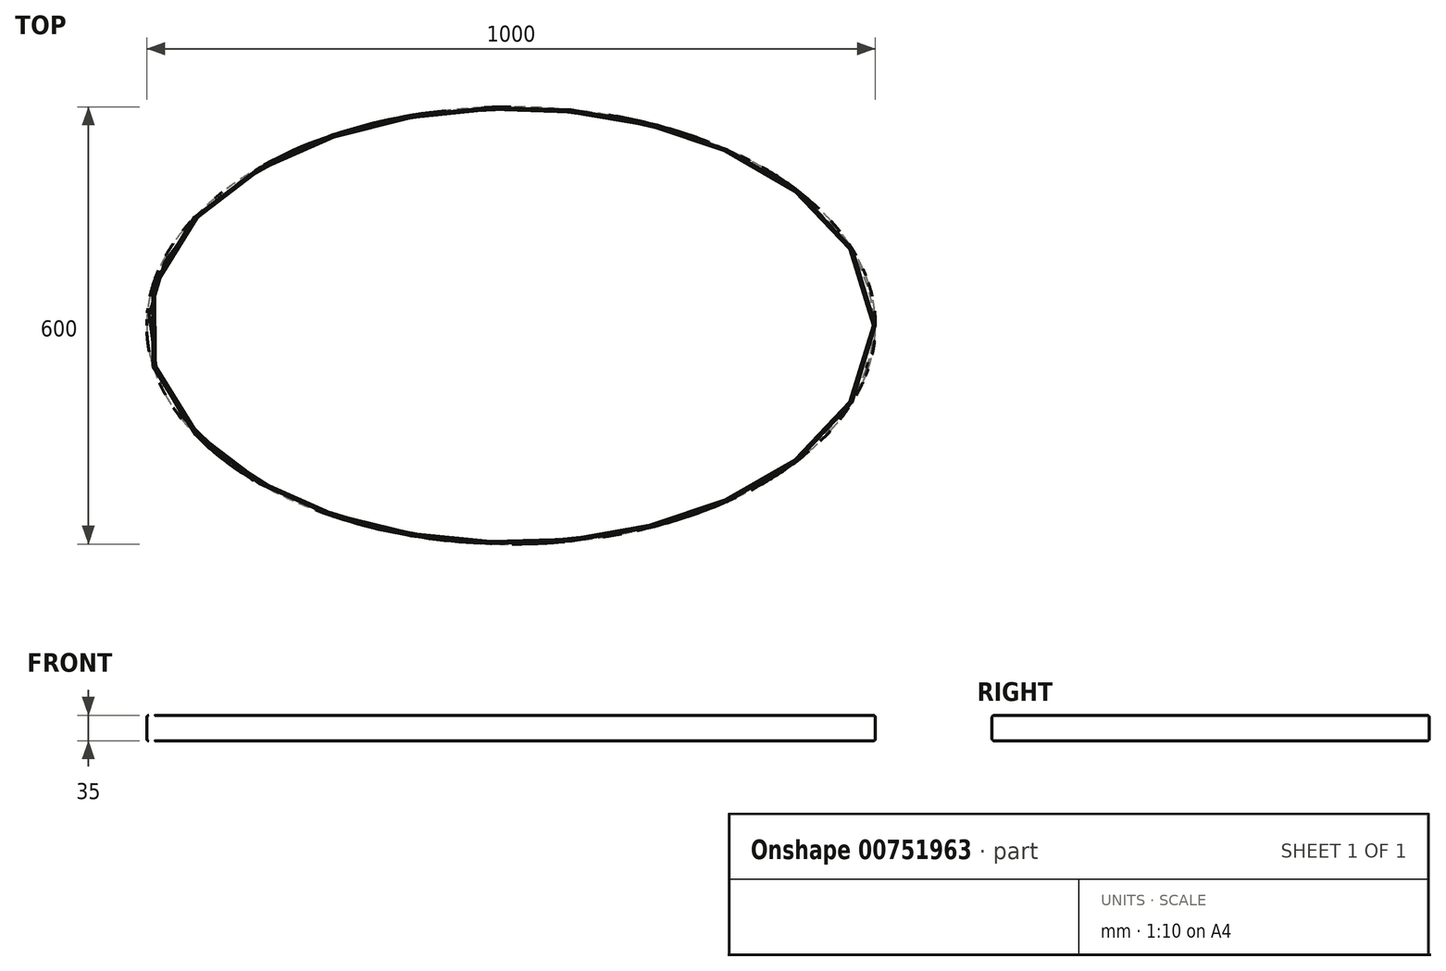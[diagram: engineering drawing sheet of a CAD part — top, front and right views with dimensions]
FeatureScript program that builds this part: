
annotation { "Feature Type Name" : "Feature", "Feature Type Description" : "" }
export const myFeature = defineFeature(function(context is Context, id is Id, definition is map)
    precondition{}
    {
        {
            var Q0;
            Q0=qCreatedBy(makeId("Top.planeOp"),FACE);
            var sketch = newSketch(context, id + "F0", { "sketchPlane" : qUnion([Q0])});
            skEllipse(sketch, "E0", {"center": v(0, 0) * mm, "majorRadius": 500 * mm, "minorRadius": 300 * mm, "majorAxis": v(1, 0)});
            skSolve(sketch);
        }
        {
            var Q0;
            Q0=makeQuery(id+"F0.imprint","IMPRINT",FACE,{"disambiguationData":[TD([[makeQuery(id+"F0.imprint","IMPRINT",EDGE,{"derivedFrom":sQuery(id+"F0.wireOp",EDGE,"E0")}),1.0]])]});
            var Q1;
            Q1=sQuery(id+"F0.wireOp",EDGE,"E0");
            extrude(context, id + "F1", {"entities" : qUnion([Q0]), "surfaceEntities" : qUnion([Q1]), "oppositeDirection" : true, "depth" : 35 * mm, "offsetDistance" : 25 * mm});
        }
        {
            var Q0;
            Q0=makeQuery(id+"F1.opExtrude","CAP_EDGE",EDGE,{"disambiguationData":[OSD([sQuery(id+"F0.wireOp",EDGE,"E0")])],"isStart":false});
            var Q1;
            Q1=makeQuery(id+"F1.opExtrude","CAP_EDGE",EDGE,{"disambiguationData":[OSD([sQuery(id+"F0.wireOp",EDGE,"E0")])],"isStart":true});
            fillet(context, id + "F2", {"entities" : qUnion([Q0, Q1]), "radius" : 3 * mm, "tangentPropagation" : true, "allowEdgeOverflow" : false});
        }
    });
